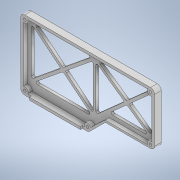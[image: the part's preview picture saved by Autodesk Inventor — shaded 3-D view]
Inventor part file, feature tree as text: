
AUTODESK INVENTOR PART (.ipt)
format: ipt  version: 2021 (Build 250183000, 183)  size: 493,056 bytes
history: native  units: mm
features: sketch x19, extrude x17, fillet x5, hole x2, chamfer x2
ambient origin geometry x8: Origin, YZ Plane, XZ Plane, XY Plane, X Axis, Y Axis, Z Axis, Center Point
bodies: Solid1 (feature_tree)
feature tree (45):
  extrude  "Extrusion1"  Depth=100.0mm
  extrude  "Extrusion2"  Depth=50.0mm
  hole  "Hole1"  [1 undecoded]
  extrude  "Extrusion3"  Depth=50.0mm
  extrude  "Extrusion4"  Depth=3.0mm
  extrude  "Extrusion5"  Depth=3.0mm
  fillet  "Fillet1"  Radius=49.0mm
  extrude  "Extrusion6"  Depth=49.0mm
  extrude  "Extrusion7"  Depth=5.0mm
  extrude  "Extrusion8"  Depth=5.0mm
  chamfer  "Chamfer1"  Distance=3.0mm
  extrude  "Extrusion9"  Depth=12.5mm
  fillet  "Fillet2"  Radius=63.1mm
  extrude  "Extrusion11"  Depth=3.0mm
  extrude  "Extrusion12"  Depth=2.0mm
  chamfer  "Chamfer2"  Distance=2.0mm
  extrude  "Extrusion13"  Depth=1.5mm
  extrude  "Extrusion14"  Depth=3.0mm TaperAngle=0.0deg
  extrude  "Extrusion15"  Depth=3.0mm
  fillet  "Fillet3"  Radius=7.6mm
  fillet  "Fillet4"  Radius=46.4mm
  hole  "Hole2"  [1 undecoded]
  extrude  "Extrusion20"  Depth=3.0mm TaperAngle=0.0deg
  extrude  "Extrusion21"  Depth=5.0mm
  fillet  "Fillet5"  Radius=2.0mm
  extrude  "Extrusion22"  Depth=12.0mm TaperAngle=0.0deg
  sketch  "Sketch1"  dims[d0=52.0mm d1=100.0mm]
  sketch  "Sketch2"  dims[d2=26.0mm d3=50.0mm]
  sketch  "Sketch3"  dims[d4=2.0mm d5=0.0mm d6=3.0mm]
  sketch  "Sketch4"  dims[d7=3.0mm d8=50.0mm]
  sketch  "Sketch5"  dims[d9=3.0mm d10=97.0mm]
  sketch  "Sketch6"  dims[d11=15.0mm d12=3.0mm d13=49.0mm]
  sketch  "Sketch7"  dims[d14=97.0mm d15=49.0mm]
  sketch  "Sketch8"  dims[d16=2.0mm d17=5.0mm]
  sketch  "Sketch9"  dims[d18=2.0mm d19=5.0mm]
  sketch  "Sketch10"  dims[d20=2.0mm]
  sketch  "Sketch12"  dims[d21=5.0mm]
  sketch  "Sketch13"  dims[d22=2.0mm]
  sketch  "Sketch14"  dims[d23=5.0mm]
  sketch  "Sketch15"  dims[d24=2.0mm]
  sketch  "Sketch16"  dims[d25=5.0mm d26=3.0mm d27=0.0mm]
  sketch  "Sketch17"  dims[d28=2.0mm d29=6.0mm d30=5.0mm d31=2.0mm d32=90.0deg d33=10.0mm d34=20.594885mm d35=12.5mm d36=63.1mm]
  sketch  "Sketch23"  dims[d37=3.0mm d38=0.0mm d39=50.673mm]
  sketch  "Sketch24"  dims[d40=3.0mm d41=0.0mm d42=2.0mm]
  sketch  "Sketch25"  dims[d43=2.0mm d44=2.0mm d45=1.5mm d46=3.0mm d47=0.0mm d48=3.0mm d49=7.6mm d50=46.4mm d51=6.7mm d52=3.0mm d53=0.0mm d54=5.0mm d55=2.0mm d56=12.0mm d57=0.0mm d58=1.4mm d59=1.2mm d60=3.0mm d61=14.0mm d62=1.2mm d63=1.4mm d64=12.0mm d65=3.0mm d66=0.0mm d67=1.0mm d68=2.0mm d69=45.0deg d70=1.2mm d71=3.0mm d72=0.0mm d73=1.0mm d77=3.0mm d78=0.0mm d79=3.0mm d80=3.0mm d81=3.0mm d82=3.0mm d83=3.0mm d84=3.0mm d85=3.0mm d86=48.0mm d87=2.0mm d88=0.0mm d89=8.4mm d90=2.0mm d91=45.0deg d92=1.2mm d93=3.0mm d94=0.0mm d95=7.6mm d96=5.0mm d97=0.0mm d98=2.0mm d99=2.0mm d100=2.0mm d101=2.0mm d102=2.0mm d103=2.0mm d104=0.0mm d105=1.0mm d106=1.0mm d107=2.0mm d108=6.0mm d109=5.0mm d110=2.0mm d111=90.0deg d112=4.0mm d113=20.594885mm d146=6.5mm d147=5.0mm d148=2.0mm d149=0.0mm d150=0.3mm d151=0.3mm d152=2.0mm d153=0.0mm d154=3.0mm d155=2.0mm d156=2.0mm d157=2.0mm d158=2.0mm d159=0.0mm d74=0.872665mm d75=0.872665mm d76=0.5mm d114=0.75mm d115=20.594885mm d116=0.0625mm d117=0.75mm d118=0.375mm]
note: 2 required parameter values undecoded (feature->parameter linkage not recoverable at this tier; creation-order binding heuristic only, values carry confidence <= 0.55)
